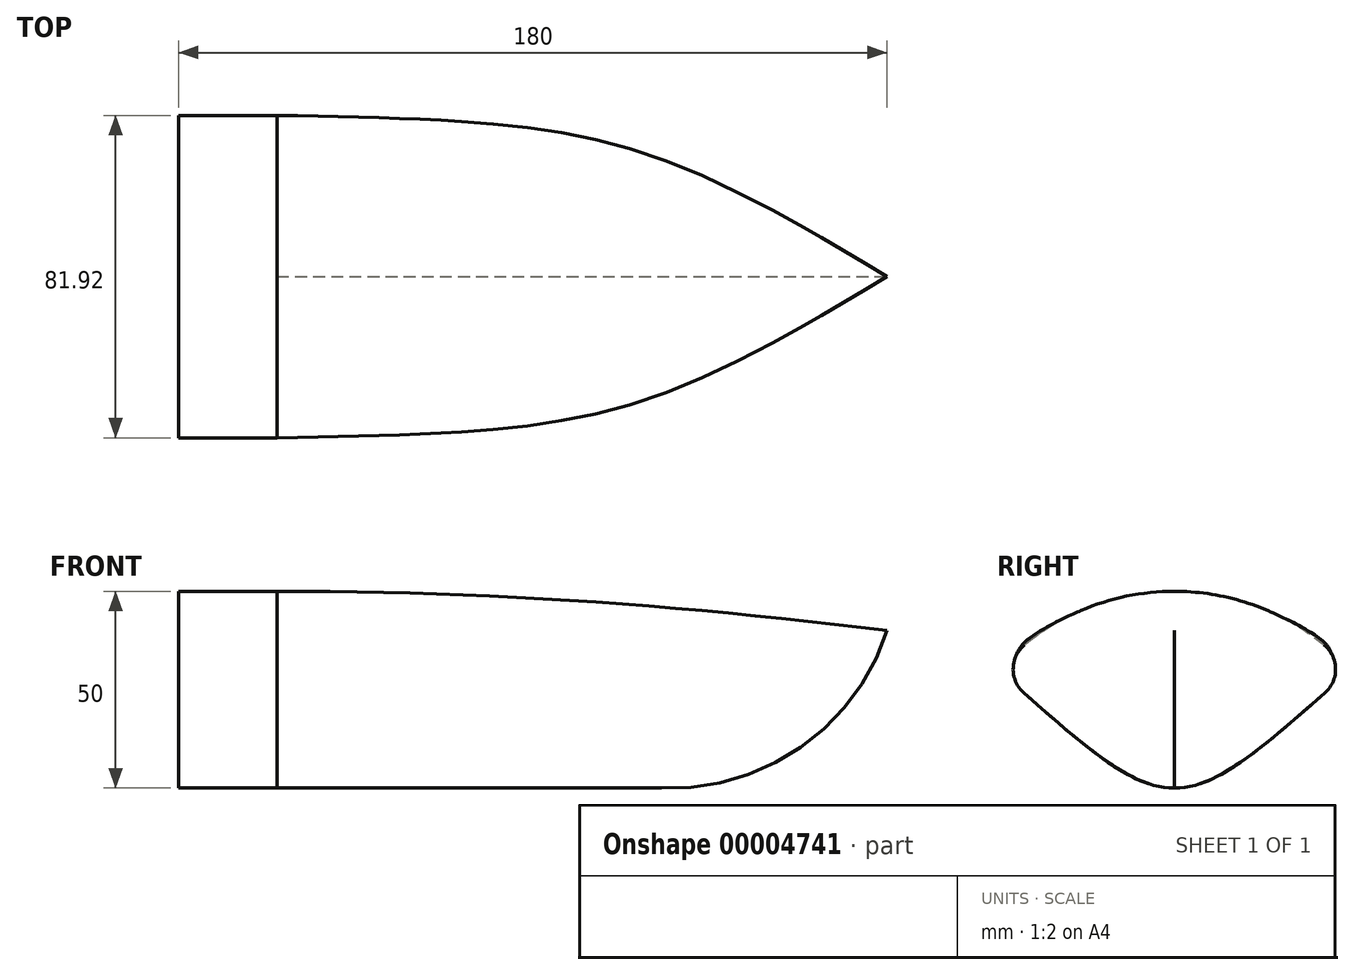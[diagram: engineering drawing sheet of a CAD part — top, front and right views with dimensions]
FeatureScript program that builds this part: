
annotation { "Feature Type Name" : "Feature", "Feature Type Description" : "" }
export const myFeature = defineFeature(function(context is Context, id is Id, definition is map)
    precondition{}
    {
        {
            var Q0;
            Q0=qCreatedBy(makeId("Right.planeOp"),FACE);
            cPlane(context, id + "F0", {"entities" : qUnion([Q0]), "cplaneType" : CPlaneType.OFFSET, "offset" : 180 * mm, "width" : 150 * mm, "height" : 150 * mm});
        }
        {
            var Q0;
            Q0=qCreatedBy(makeId("Right.planeOp"),FACE);
            var sketch = newSketch(context, id + "F1", { "sketchPlane" : qUnion([Q0])});
            skArc(sketch, "E0", {"start": v(44.72, 0) * mm, "mid": v(0, 20) * mm, "end": v(-44.72, 0) * mm});
            skFitSpline(sketch, "E1", {"points": [v(-44.72, 0) * mm, v(44.72, 0) * mm], "startDerivative": vector(134.16, -120) * mm, "endDerivative": vector(134.16, 120) * mm});
            skArc(sketch, "E2", {"start": v(-38.03, 6.4) * mm, "mid": v(-40.96, 0.38) * mm, "end": v(-38.27, -5.76) * mm});
            skLineSegment(sketch, "E3", {"start": v(0, 20) * mm, "end": v(0, 0) * mm, "construction": true});
            skArc(sketch, "E4.0.MirrorCS", {"start": v(38.03, 6.4) * mm, "mid": v(40.96, 0.38) * mm, "end": v(38.27, -5.76) * mm});
            skSolve(sketch);
        }
        {
            var Q0;
            {var subQ1=sQuery(id+"F1.wireOp",EDGE,"E2");Q0=makeQuery(id+"F1.imprint","IMPRINT",FACE,{"disambiguationData":[TD([[makeQuery(id+"F1.imprint","IMPRINT",EDGE,{"derivedFrom":subQ1}),1.0]])]});}
            extrude(context, id + "F2", {"entities" : qUnion([Q0]), "depth" : 25 * mm});
        }
        {
            var Q0;
            Q0=qCreatedBy(id+"F0.planeOp",FACE);
            var sketch = newSketch(context, id + "F3", { "sketchPlane" : qUnion([Q0])});
            skPoint(sketch, "E5", {"position": v(0, 10) * mm});
            skSolve(sketch);
        }
        {
            var Q0;
            Q0=makeQuery(id+"F2.opExtrude","CAP_VERTEX",VERTEX,{"disambiguationData":[OSD([sQuery(id+"F1.wireOp",EDGE,"E0"),sQuery(id+"F1.wireOp",EDGE,"E4.0.MirrorCS")])],"isStart":false});
            var Q1;
            Q1=makeQuery(id+"F2.opExtrude","CAP_VERTEX",VERTEX,{"disambiguationData":[OSD([sQuery(id+"F1.wireOp",EDGE,"E0"),sQuery(id+"F1.wireOp",EDGE,"E2")])],"isStart":false});
            var Q2;
            Q2=sQuery(id+"F3.wireOp",VERTEX,"E5");
            cPlane(context, id + "F4", {"entities" : qUnion([Q0, Q1, Q2]), "cplaneType" : CPlaneType.THREE_POINT, "offset" : 150 * mm, "width" : 150 * mm, "height" : 150 * mm});
        }
        {
            var Q0;
            Q0=qCreatedBy(id+"F4.planeOp",FACE);
            var sketch = newSketch(context, id + "F5", { "sketchPlane" : qUnion([Q0])});
            skFitSpline(sketch, "E6", {"points": [v(25.14, -38.03) * mm, v(180.18, 0) * mm], "startDerivative": vector(240, 0) * mm, "endDerivative": vector(193.93, 114.08) * mm});
            skLineSegment(sketch, "E7", {"start": v(105.14, -38.03) * mm, "end": v(115.54, -38.03) * mm, "construction": true});
            skLineSegment(sketch, "E8", {"start": v(180.18, 0) * mm, "end": v(148.05, 0) * mm, "construction": true});
            skFitSpline(sketch, "E9.0.MirrorCS", {"points": [v(25.14, 38.03) * mm, v(180.18, 0) * mm], "startDerivative": vector(240, 0) * mm, "endDerivative": vector(193.93, -114.08) * mm});
            skSolve(sketch);
        }
        {
            var Q0;
            Q0=qCreatedBy(makeId("Front.planeOp"),FACE);
            var sketch = newSketch(context, id + "F6", { "sketchPlane" : qUnion([Q0])});
            skFitSpline(sketch, "E10", {"points": [v(25, 20) * mm, v(180, 10) * mm], "startDerivative": vector(60, 0) * mm, "endDerivative": vector(238.12, -30) * mm});
            skLineSegment(sketch, "E11.0", {"start": v(25, 20) * mm, "end": v(25, 6.4) * mm});
            skSolve(sketch);
        }
        {
            var Q0;
            Q0=qCreatedBy(makeId("Front.planeOp"),FACE);
            var sketch = newSketch(context, id + "F7", { "sketchPlane" : qUnion([Q0])});
            skFitSpline(sketch, "E12", {"points": [v(25, -30) * mm, v(180, 10) * mm], "startDerivative": vector(300, 0) * mm, "endDerivative": vector(30, 120) * mm, "construction": true});
            skLineSegment(sketch, "E13", {"start": v(25, -30) * mm, "end": v(125, -30) * mm});
            skArc(sketch, "E14", {"start": v(125, -30) * mm, "mid": v(159, -18.94) * mm, "end": v(180, 10) * mm});
            skSolve(sketch);
        }
        {
            var Q1;
            Q1=makeQuery(id+"F2.opExtrude","CAP_FACE",FACE,{"disambiguationData":[OSD([sQuery(id+"F1.wireOp",EDGE,"E0"),sQuery(id+"F1.wireOp",EDGE,"E1"),sQuery(id+"F1.wireOp",EDGE,"E2"),sQuery(id+"F1.wireOp",EDGE,"E4.0.MirrorCS")])],"isStart":false});
            var Q2;
            Q2=sQuery(id+"F3.wireOp",VERTEX,"E5");
            var Q3;
            Q3=sQuery(id+"F5.wireOp",EDGE,"E9.0.MirrorCS");
            var Q4;
            Q4=sQuery(id+"F5.wireOp",EDGE,"E6");
            var Q5;
            Q5=sQuery(id+"F6.wireOp",EDGE,"E10");
            var Q6;
            Q6 = qConstructionFilter(qBodyType(qCreatedBy(id + "F7" ,EDGE), BodyType.WIRE), ConstructionObject.NO);
            loft(context, id + "F8", {"operationType" : NewBodyOperationType.ADD, "addGuides" : true, "sheetProfilesArray" : [{ "sheetProfileEntities" : qUnion([Q1]) }, { "sheetProfileEntities" : qUnion([Q2]) }], "guidesArray" : [{ "guideEntities" : qUnion([Q3]), "guideDerivativeType" : LoftGuideDerivativeType.DEFAULT, "guideDerivativeMagnitude" : 1 }, { "guideEntities" : qUnion([Q4]), "guideDerivativeType" : LoftGuideDerivativeType.DEFAULT, "guideDerivativeMagnitude" : 1 }, { "guideEntities" : qUnion([Q5]), "guideDerivativeType" : LoftGuideDerivativeType.DEFAULT, "guideDerivativeMagnitude" : 1 }, { "guideEntities" : qUnion([Q6]), "guideDerivativeType" : LoftGuideDerivativeType.DEFAULT, "guideDerivativeMagnitude" : 1 }]});
        }
    });
